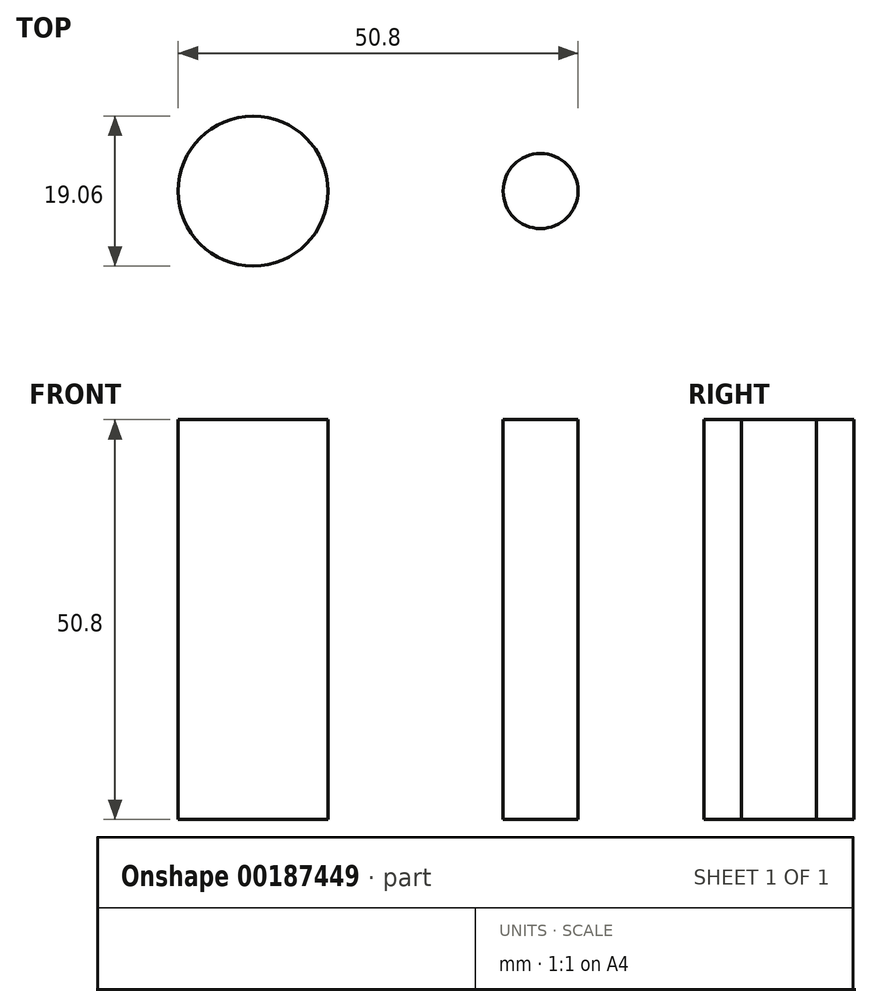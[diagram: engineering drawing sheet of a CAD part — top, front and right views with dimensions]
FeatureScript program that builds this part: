
annotation { "Feature Type Name" : "Feature", "Feature Type Description" : "" }
export const myFeature = defineFeature(function(context is Context, id is Id, definition is map)
    precondition{}
    {
        {
            var Q0;
            Q0=qCreatedBy(makeId("Top.planeOp"),FACE);
            var sketch = newSketch(context, id + "F0", { "sketchPlane" : qUnion([Q0])});
            skCircle(sketch, "E0", {"center": v(-18.7, 0) * mm, "radius": 12.7 * mm});
            skCircle(sketch, "E1", {"center": v(17.8, 0) * mm, "radius": 7.94 * mm});
            skLineSegment(sketch, "E2", {"start": v(-17.05, 12.6) * mm, "end": v(18.84, 7.87) * mm});
            skLineSegment(sketch, "E3", {"start": v(-17.05, -12.6) * mm, "end": v(18.84, -7.87) * mm});
            skCircle(sketch, "E4", {"center": v(-18.7, 0) * mm, "radius": 9.53 * mm});
            skCircle(sketch, "E5", {"center": v(17.8, 0) * mm, "radius": 4.76 * mm});
            skSolve(sketch);
        }
        {
            var Q0;
            Q0=makeQuery(id+"F0.imprint","IMPRINT",FACE,{"disambiguationData":[TD([[makeQuery(id+"F0.imprint","IMPRINT",EDGE,{"derivedFrom":sQuery(id+"F0.wireOp",EDGE,"E4")}),1.0]])]});
            var Q1;
            Q1=makeQuery(id+"F0.imprint","IMPRINT",FACE,{"disambiguationData":[TD([[makeQuery(id+"F0.imprint","IMPRINT",EDGE,{"derivedFrom":sQuery(id+"F0.wireOp",EDGE,"E5")}),1.0]])]});
            extrude(context, id + "F1", {"entities" : qUnion([Q0, Q1]), "depth" : 50.8 * mm});
        }
    });
